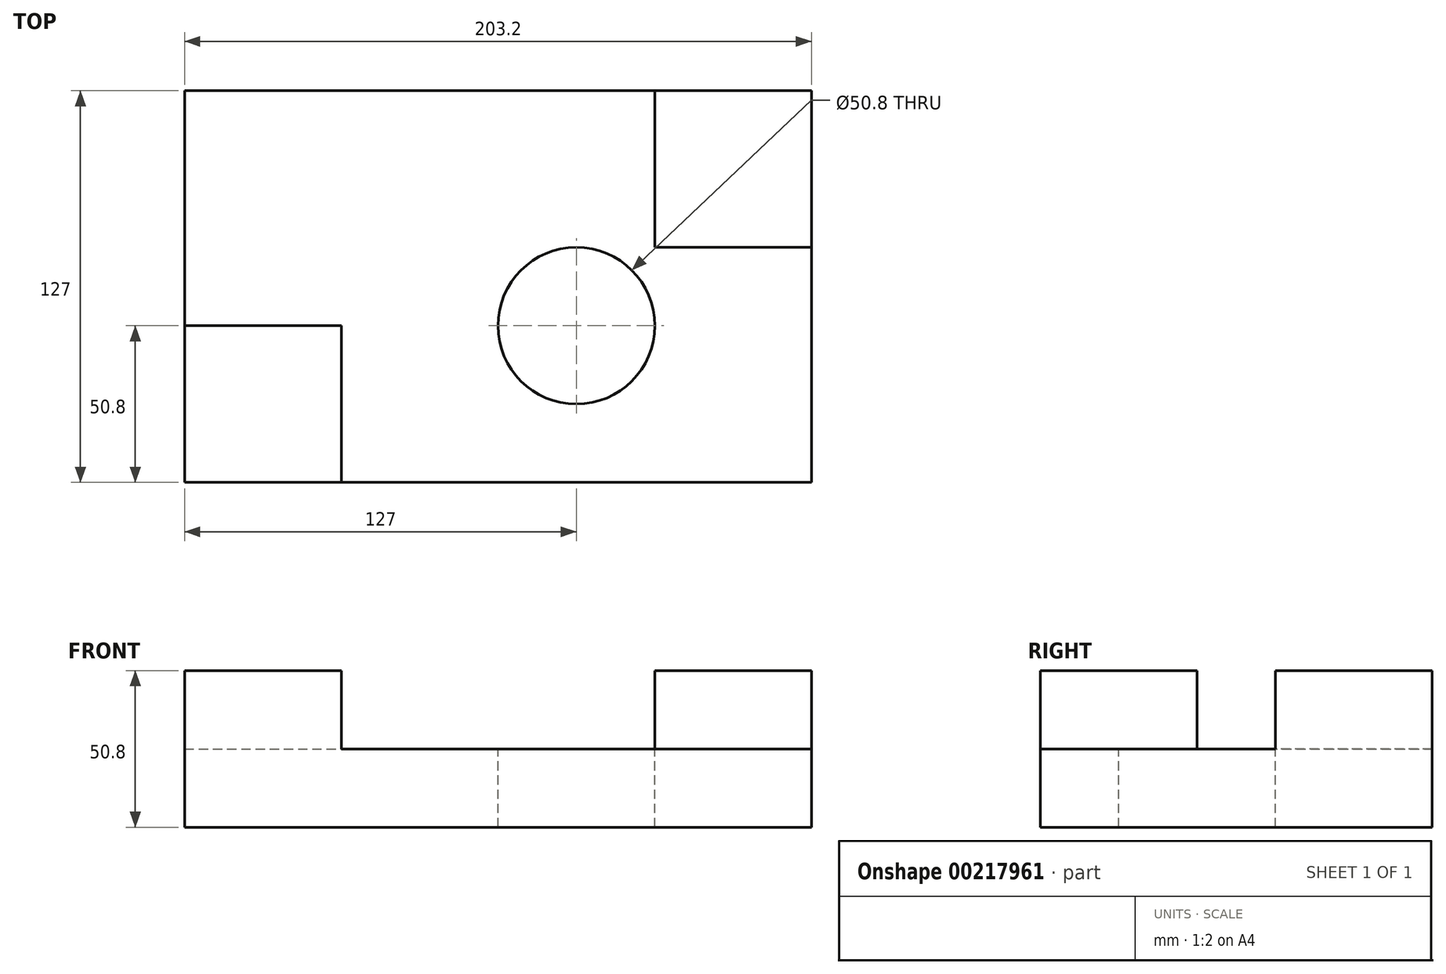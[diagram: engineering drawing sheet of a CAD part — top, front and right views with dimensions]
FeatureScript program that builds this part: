
annotation { "Feature Type Name" : "Feature", "Feature Type Description" : "" }
export const myFeature = defineFeature(function(context is Context, id is Id, definition is map)
    precondition{}
    {
        {
            var Q0;
            Q0=qCreatedBy(makeId("Top.planeOp"),FACE);
            var sketch = newSketch(context, id + "F0", { "sketchPlane" : qUnion([Q0])});
            skLineSegment(sketch, "E0.bottom", {"start": v(0, 0) * mm, "end": v(203.2, 0) * mm});
            skLineSegment(sketch, "E0.top", {"start": v(0, 127) * mm, "end": v(203.2, 127) * mm});
            skLineSegment(sketch, "E0.left", {"start": v(0, 0) * mm, "end": v(0, 127) * mm});
            skLineSegment(sketch, "E0.right", {"start": v(203.2, 0) * mm, "end": v(203.2, 127) * mm});
            skSolve(sketch);
        }
        {
            var Q0;
            Q0 = qSketchRegion(id + "F0", true);
            extrude(context, id + "F1", {"entities" : qUnion([Q0]), "depth" : 25.4 * mm});
        }
        {
            var Q0;
            Q0=makeQuery(id+"F1.opExtrude","CAP_FACE",FACE,{"disambiguationData":[OSD([sQuery(id+"F0.wireOp",EDGE,"E0.bottom"),sQuery(id+"F0.wireOp",EDGE,"E0.top"),sQuery(id+"F0.wireOp",EDGE,"E0.left"),sQuery(id+"F0.wireOp",EDGE,"E0.right")])],"isStart":false});
            var sketch = newSketch(context, id + "F2", { "sketchPlane" : qUnion([Q0])});
            skLineSegment(sketch, "E1.bottom", {"start": v(0, 0) * mm, "end": v(50.8, 0) * mm});
            skLineSegment(sketch, "E1.top", {"start": v(0, 50.8) * mm, "end": v(50.8, 50.8) * mm});
            skLineSegment(sketch, "E1.left", {"start": v(0, 0) * mm, "end": v(0, 50.8) * mm});
            skLineSegment(sketch, "E1.right", {"start": v(50.8, 0) * mm, "end": v(50.8, 50.8) * mm});
            skLineSegment(sketch, "E2.bottom", {"start": v(203.2, 127) * mm, "end": v(152.4, 127) * mm});
            skLineSegment(sketch, "E2.top", {"start": v(203.2, 76.2) * mm, "end": v(152.4, 76.2) * mm});
            skLineSegment(sketch, "E2.left", {"start": v(203.2, 127) * mm, "end": v(203.2, 76.2) * mm});
            skLineSegment(sketch, "E2.right", {"start": v(152.4, 127) * mm, "end": v(152.4, 76.2) * mm});
            skSolve(sketch);
        }
        {
            var Q0;
            Q0 = qSketchRegion(id + "F2", true);
            extrude(context, id + "F3", {"entities" : qUnion([Q0]), "operationType" : NewBodyOperationType.ADD, "depth" : 25.4 * mm});
        }
        {
            var Q0;
            Q0=makeQuery(id+"F1.opExtrude","CAP_FACE",FACE,{"disambiguationData":[OSD([sQuery(id+"F0.wireOp",EDGE,"E0.bottom"),sQuery(id+"F0.wireOp",EDGE,"E0.top"),sQuery(id+"F0.wireOp",EDGE,"E0.left"),sQuery(id+"F0.wireOp",EDGE,"E0.right")])],"isStart":false});
            var sketch = newSketch(context, id + "F4", { "sketchPlane" : qUnion([Q0])});
            skCircle(sketch, "E3", {"center": v(127, 50.8) * mm, "radius": 25.4 * mm});
            skSolve(sketch);
        }
        {
            var Q0;
            Q0 = qSketchRegion(id + "F4", true);
            extrude(context, id + "F5", {"entities" : qUnion([Q0]), "operationType" : NewBodyOperationType.REMOVE, "endBound" : BoundingType.THROUGH_ALL, "oppositeDirection" : true, "depth" : 25.4 * mm});
        }
    });
